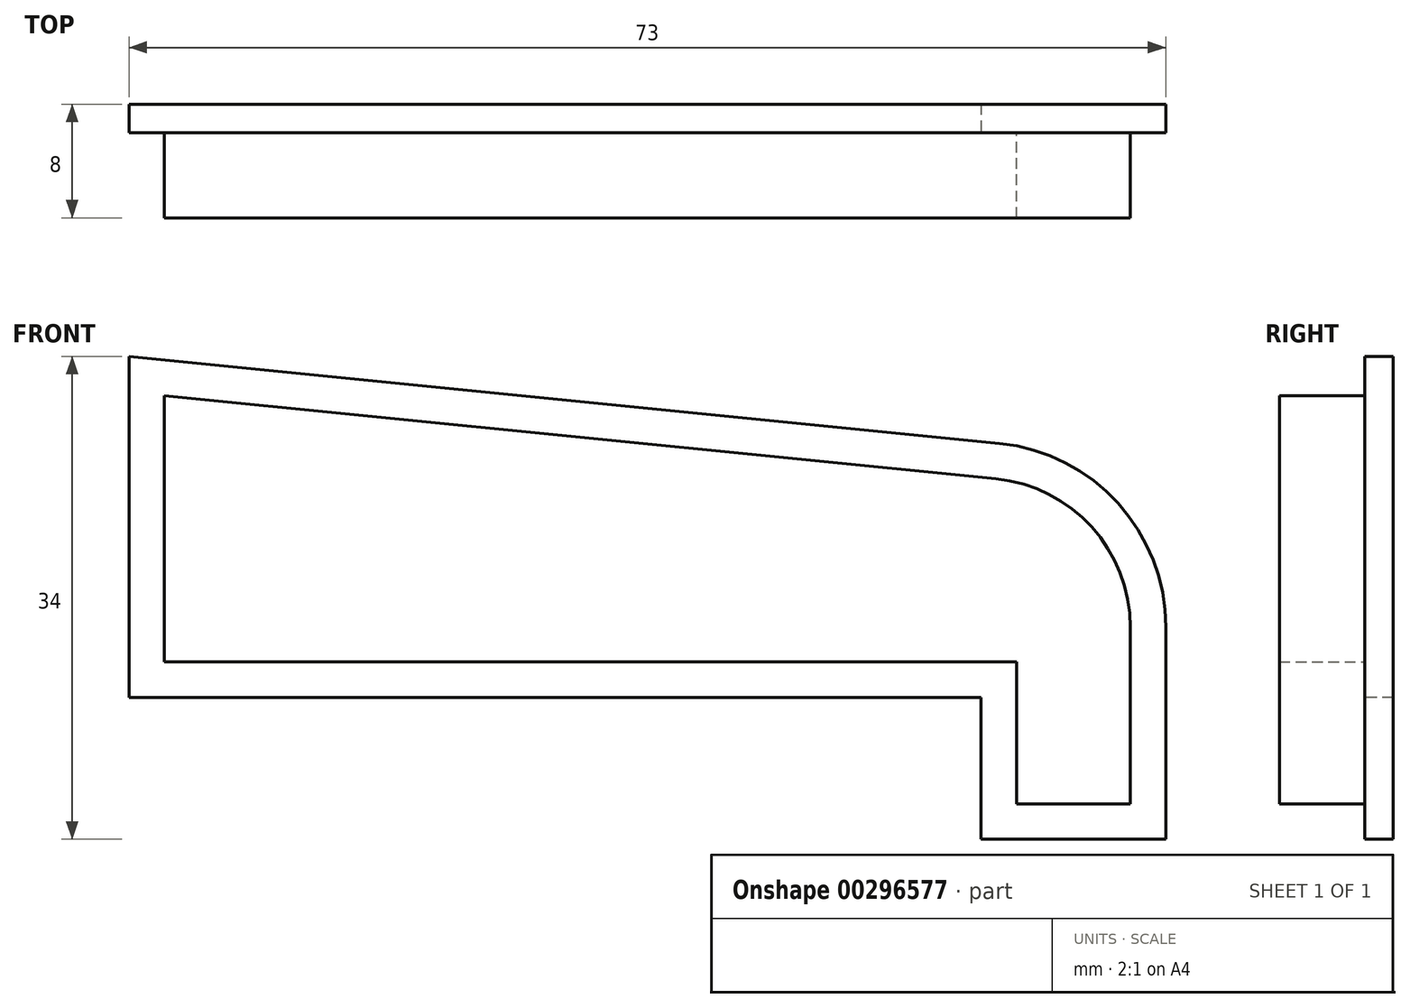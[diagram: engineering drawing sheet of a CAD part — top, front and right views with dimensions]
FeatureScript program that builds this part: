
annotation { "Feature Type Name" : "Feature", "Feature Type Description" : "" }
export const myFeature = defineFeature(function(context is Context, id is Id, definition is map)
    precondition{}
    {
        {
            var Q0;
            Q0=qCreatedBy(makeId("Front.planeOp"),FACE);
            var sketch = newSketch(context, id + "F0", { "sketchPlane" : qUnion([Q0])});
            skLineSegment(sketch, "E0", {"start": v(0, 0) * mm, "end": v(0, 24) * mm});
            skLineSegment(sketch, "E1", {"start": v(0, 24) * mm, "end": v(61.3, 17.87) * mm});
            skArc(sketch, "E2", {"start": v(61.3, 17.87) * mm, "mid": v(69.64, 13.66) * mm, "end": v(73, 4.94) * mm});
            skLineSegment(sketch, "E3", {"start": v(73, 4.94) * mm, "end": v(73, -10) * mm});
            skLineSegment(sketch, "E4", {"start": v(73, -10) * mm, "end": v(60, -10) * mm});
            skLineSegment(sketch, "E5", {"start": v(60, -10) * mm, "end": v(60, 0) * mm});
            skLineSegment(sketch, "E6", {"start": v(60, 0) * mm, "end": v(0, 0) * mm});
            skLineSegment(sketch, "E7", {"start": v(60, 0) * mm, "end": v(60, 18) * mm, "construction": true});
            skLineSegment(sketch, "E8.0", {"start": v(2.5, 2.5) * mm, "end": v(2.5, 21.24) * mm});
            skLineSegment(sketch, "E8.1", {"start": v(62.5, 2.5) * mm, "end": v(2.5, 2.5) * mm});
            skArc(sketch, "E8.2", {"start": v(61.04, 15.38) * mm, "mid": v(67.79, 11.98) * mm, "end": v(70.5, 4.94) * mm});
            skLineSegment(sketch, "E8.3", {"start": v(70.5, 4.94) * mm, "end": v(70.5, -7.5) * mm});
            skLineSegment(sketch, "E8.4", {"start": v(70.5, -7.5) * mm, "end": v(62.5, -7.5) * mm});
            skLineSegment(sketch, "E8.5", {"start": v(2.5, 21.24) * mm, "end": v(61.04, 15.38) * mm});
            skLineSegment(sketch, "E8.6", {"start": v(62.5, -7.5) * mm, "end": v(62.5, 2.5) * mm});
            skSolve(sketch);
        }
        {
            var Q0;
            Q0=makeQuery(id+"F0.imprint","IMPRINT",FACE,{"disambiguationData":[TD([[makeQuery(id+"F0.imprint","IMPRINT",EDGE,{"derivedFrom":sQuery(id+"F0.wireOp",EDGE,"E0")}),-1.0]])]});
            var Q1;
            Q1=makeQuery(id+"F0.imprint","IMPRINT",FACE,{"disambiguationData":[TD([[makeQuery(id+"F0.imprint","IMPRINT",EDGE,{"derivedFrom":sQuery(id+"F0.wireOp",EDGE,"E8.0")}),-1.0]])]});
            extrude(context, id + "F1", {"entities" : qUnion([Q0, Q1]), "oppositeDirection" : true, "depth" : (2) * mm});
        }
        {
            var Q0;
            Q0=makeQuery(id+"F0.imprint","IMPRINT",FACE,{"disambiguationData":[TD([[makeQuery(id+"F0.imprint","IMPRINT",EDGE,{"derivedFrom":sQuery(id+"F0.wireOp",EDGE,"E8.0")}),-1.0]])]});
            extrude(context, id + "F2", {"entities" : qUnion([Q0]), "operationType" : NewBodyOperationType.ADD, "depth" : (6) * mm});
        }
    });
